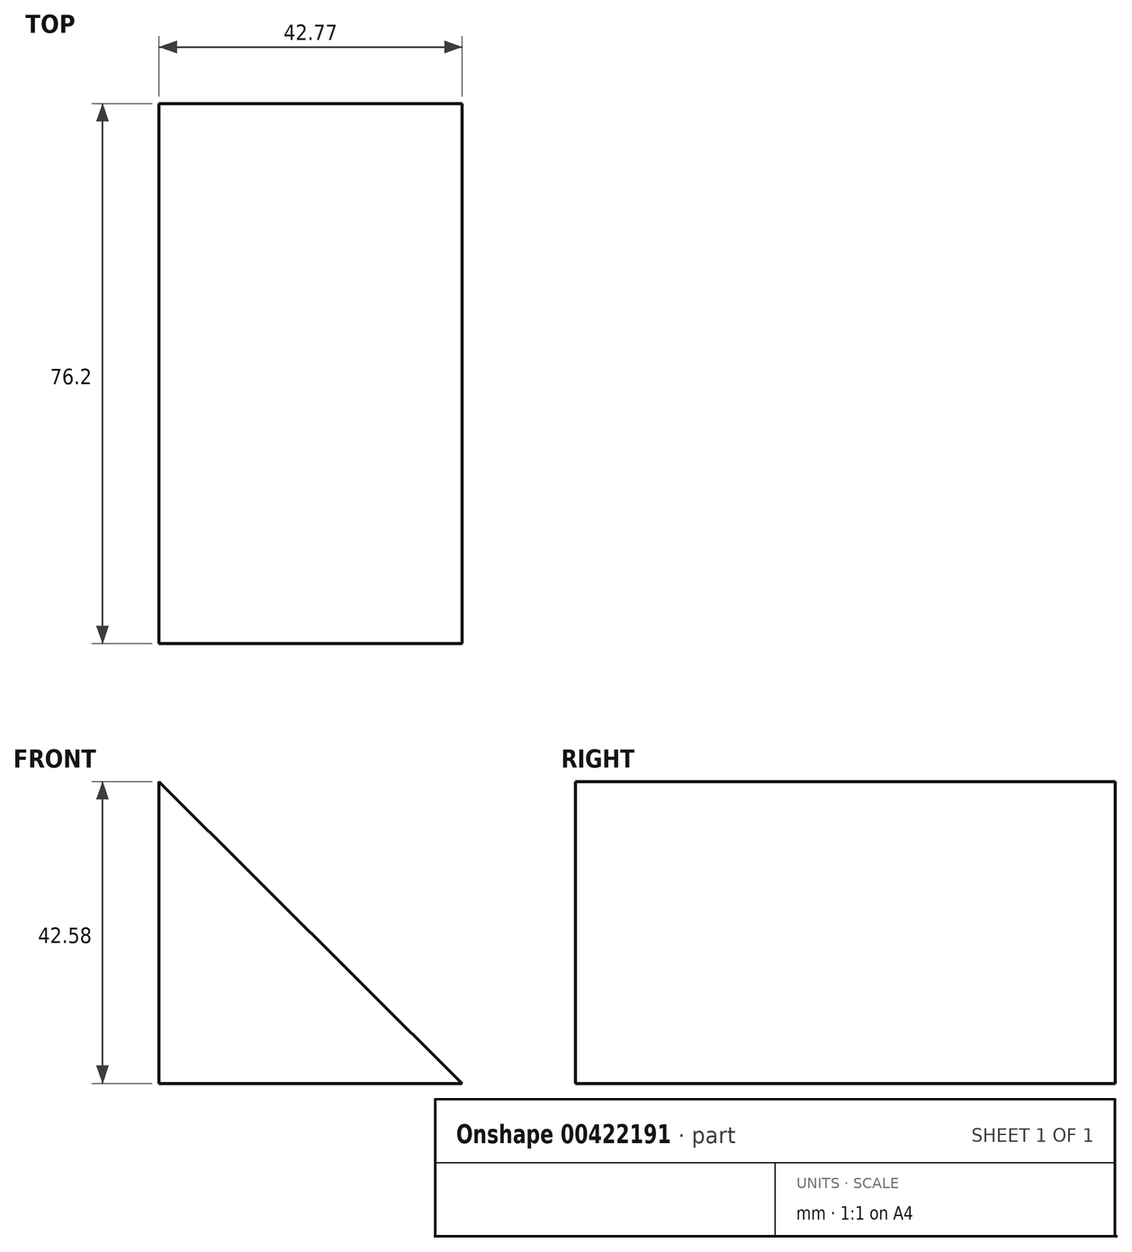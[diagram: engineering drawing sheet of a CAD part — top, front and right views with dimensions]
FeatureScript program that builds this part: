
annotation { "Feature Type Name" : "Feature", "Feature Type Description" : "" }
export const myFeature = defineFeature(function(context is Context, id is Id, definition is map)
    precondition{}
    {
        {
            var Q0;
            Q0=qCreatedBy(makeId("Front.planeOp"),FACE);
            var sketch = newSketch(context, id + "F0", { "sketchPlane" : qUnion([Q0])});
            skLineSegment(sketch, "E0", {"start": v(-42.77, 42.58) * mm, "end": v(-42.77, 0) * mm});
            skLineSegment(sketch, "E1", {"start": v(-42.77, 0) * mm, "end": v(0, 0) * mm});
            skLineSegment(sketch, "E2", {"start": v(0, 0) * mm, "end": v(-42.77, 42.58) * mm});
            skSolve(sketch);
        }
        {
            var Q0;
            Q0 = qSketchRegion(id + "F0", true);
            extrude(context, id + "F1", {"entities" : qUnion([Q0]), "depth" : 76.2 * mm});
        }
    });
